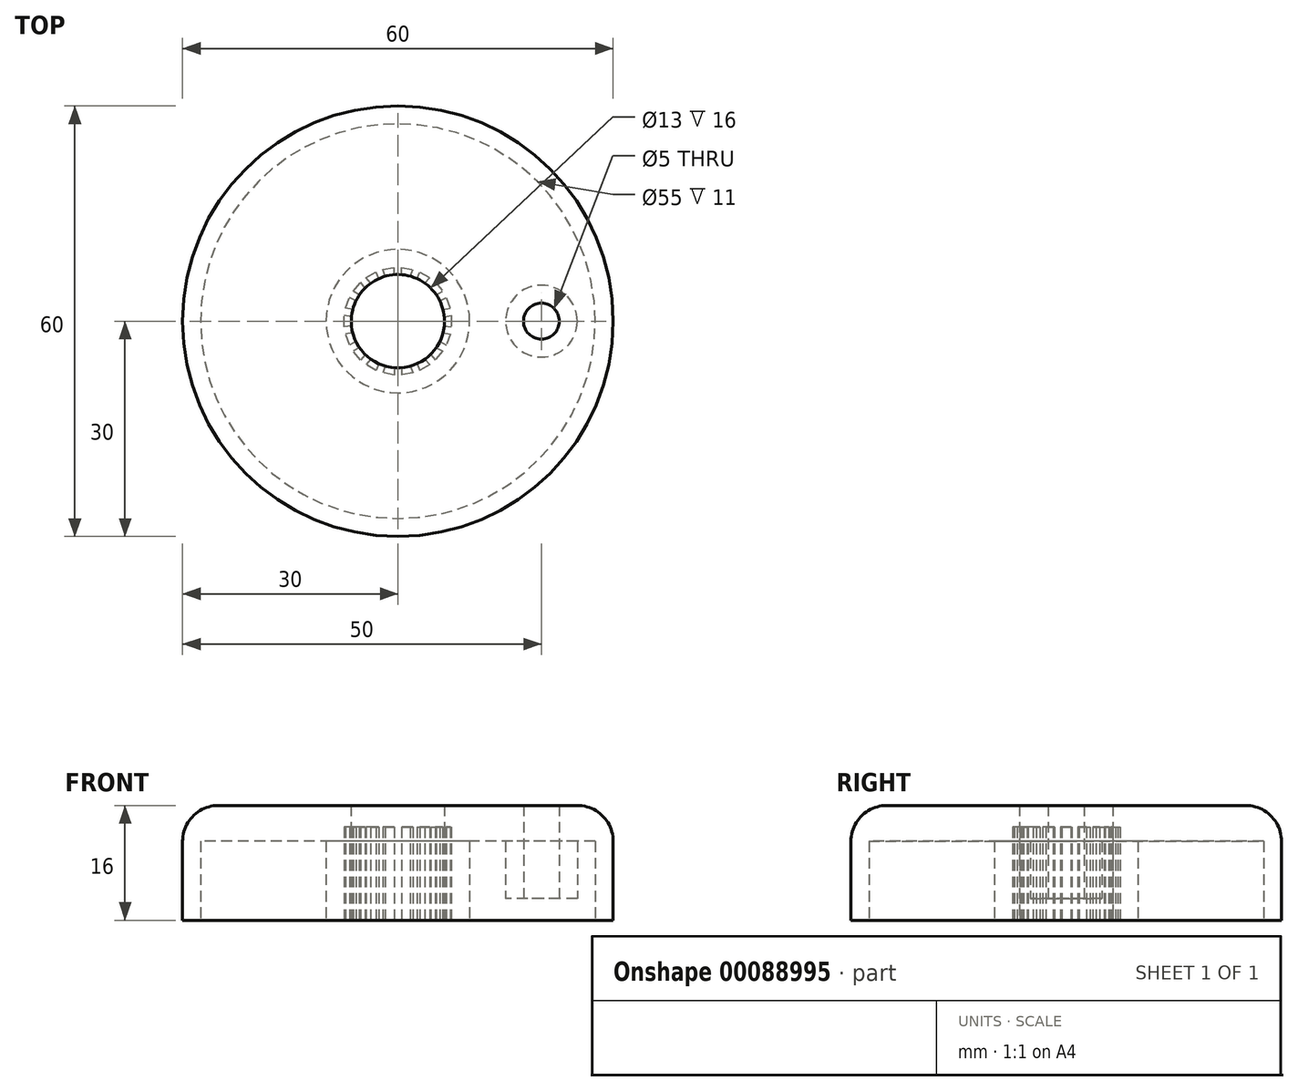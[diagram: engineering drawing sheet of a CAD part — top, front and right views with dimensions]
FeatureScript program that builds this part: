
annotation { "Feature Type Name" : "Feature", "Feature Type Description" : "" }
export const myFeature = defineFeature(function(context is Context, id is Id, definition is map)
    precondition{}
    {
        {
            var Q0;
            Q0=qCreatedBy(makeId("Top.planeOp"),FACE);
            var sketch = newSketch(context, id + "F0", { "sketchPlane" : qUnion([Q0])});
            skCircle(sketch, "E0", {"center": v(0, 0) * mm, "radius": 7.5 * mm, "construction": true});
            skLineSegment(sketch, "E1", {"start": v(0, 0) * mm, "end": v(0, 7.5) * mm, "construction": true});
            skLineSegment(sketch, "E2", {"start": v(0.5, 6.48) * mm, "end": v(0.5, 7.48) * mm});
            skLineSegment(sketch, "E3.MirrorCS", {"start": v(-0.5, 6.48) * mm, "end": v(-0.5, 7.48) * mm});
            skCircle(sketch, "E4.0", {"center": v(0, 0) * mm, "radius": 6.5 * mm, "construction": true});
            skLineSegment(sketch, "E5", {"start": v(-0.5, 6.48) * mm, "end": v(0.5, 6.48) * mm});
            skPoint(sketch, "E6.orphan", {"position": v(-0.5, 5.89) * mm});
            skPoint(sketch, "E7.orphan", {"position": v(0.5, 5.89) * mm});
            skPoint(sketch, "E8.orphan", {"position": v(0.5, 8.94) * mm});
            skPoint(sketch, "E9.orphan", {"position": v(-0.5, 8.94) * mm});
            skLineSegment(sketch, "E10.1.0", {"start": v(1.75, 6.26) * mm, "end": v(2.09, 7.2) * mm});
            skLineSegment(sketch, "E10.1.1", {"start": v(1.75, 6.26) * mm, "end": v(2.69, 5.92) * mm});
            skLineSegment(sketch, "E10.1.2", {"start": v(2.69, 5.92) * mm, "end": v(3.03, 6.86) * mm});
            skLineSegment(sketch, "E10.2.0", {"start": v(3.78, 5.29) * mm, "end": v(4.43, 6.05) * mm});
            skLineSegment(sketch, "E10.2.1", {"start": v(3.78, 5.29) * mm, "end": v(4.55, 4.64) * mm});
            skLineSegment(sketch, "E10.2.2", {"start": v(4.55, 4.64) * mm, "end": v(5.2, 5.41) * mm});
            skLineSegment(sketch, "E10.3.0", {"start": v(5.36, 3.67) * mm, "end": v(6.23, 4.17) * mm});
            skLineSegment(sketch, "E10.3.1", {"start": v(5.36, 3.67) * mm, "end": v(5.86, 2.8) * mm});
            skLineSegment(sketch, "E10.3.2", {"start": v(5.86, 2.8) * mm, "end": v(6.73, 3.3) * mm});
            skLineSegment(sketch, "E10.4.0", {"start": v(6.3, 1.62) * mm, "end": v(7.28, 1.8) * mm});
            skLineSegment(sketch, "E10.4.1", {"start": v(6.3, 1.62) * mm, "end": v(6.47, 0.63) * mm});
            skLineSegment(sketch, "E10.4.2", {"start": v(6.47, 0.63) * mm, "end": v(7.46, 0.8) * mm});
            skLineSegment(sketch, "E10.5.0", {"start": v(6.47, -0.63) * mm, "end": v(7.46, -0.8) * mm});
            skLineSegment(sketch, "E10.5.1", {"start": v(6.47, -0.63) * mm, "end": v(6.3, -1.62) * mm});
            skLineSegment(sketch, "E10.5.2", {"start": v(6.3, -1.62) * mm, "end": v(7.28, -1.8) * mm});
            skLineSegment(sketch, "E10.6.0", {"start": v(5.86, -2.8) * mm, "end": v(6.73, -3.3) * mm});
            skLineSegment(sketch, "E10.6.1", {"start": v(5.86, -2.8) * mm, "end": v(5.36, -3.67) * mm});
            skLineSegment(sketch, "E10.6.2", {"start": v(5.36, -3.67) * mm, "end": v(6.23, -4.17) * mm});
            skLineSegment(sketch, "E10.7.0", {"start": v(4.55, -4.64) * mm, "end": v(5.2, -5.41) * mm});
            skLineSegment(sketch, "E10.7.1", {"start": v(4.55, -4.64) * mm, "end": v(3.78, -5.29) * mm});
            skLineSegment(sketch, "E10.7.2", {"start": v(3.78, -5.29) * mm, "end": v(4.43, -6.05) * mm});
            skLineSegment(sketch, "E10.8.0", {"start": v(2.69, -5.92) * mm, "end": v(3.03, -6.86) * mm});
            skLineSegment(sketch, "E10.8.1", {"start": v(2.69, -5.92) * mm, "end": v(1.75, -6.26) * mm});
            skLineSegment(sketch, "E10.8.2", {"start": v(1.75, -6.26) * mm, "end": v(2.09, -7.2) * mm});
            skLineSegment(sketch, "E10.9.0", {"start": v(0.5, -6.48) * mm, "end": v(0.5, -7.48) * mm});
            skLineSegment(sketch, "E10.9.1", {"start": v(0.5, -6.48) * mm, "end": v(-0.5, -6.48) * mm});
            skLineSegment(sketch, "E10.9.2", {"start": v(-0.5, -6.48) * mm, "end": v(-0.5, -7.48) * mm});
            skLineSegment(sketch, "E10.10.0", {"start": v(-1.75, -6.26) * mm, "end": v(-2.09, -7.2) * mm});
            skLineSegment(sketch, "E10.10.1", {"start": v(-1.75, -6.26) * mm, "end": v(-2.69, -5.92) * mm});
            skLineSegment(sketch, "E10.10.2", {"start": v(-2.69, -5.92) * mm, "end": v(-3.03, -6.86) * mm});
            skLineSegment(sketch, "E10.11.0", {"start": v(-3.78, -5.29) * mm, "end": v(-4.43, -6.05) * mm});
            skLineSegment(sketch, "E10.11.1", {"start": v(-3.78, -5.29) * mm, "end": v(-4.55, -4.64) * mm});
            skLineSegment(sketch, "E10.11.2", {"start": v(-4.55, -4.64) * mm, "end": v(-5.2, -5.41) * mm});
            skLineSegment(sketch, "E10.12.0", {"start": v(-5.36, -3.67) * mm, "end": v(-6.23, -4.17) * mm});
            skLineSegment(sketch, "E10.12.1", {"start": v(-5.36, -3.67) * mm, "end": v(-5.86, -2.8) * mm});
            skLineSegment(sketch, "E10.12.2", {"start": v(-5.86, -2.8) * mm, "end": v(-6.73, -3.3) * mm});
            skLineSegment(sketch, "E10.13.0", {"start": v(-6.3, -1.62) * mm, "end": v(-7.28, -1.8) * mm});
            skLineSegment(sketch, "E10.13.1", {"start": v(-6.3, -1.62) * mm, "end": v(-6.47, -0.63) * mm});
            skLineSegment(sketch, "E10.13.2", {"start": v(-6.47, -0.63) * mm, "end": v(-7.46, -0.8) * mm});
            skLineSegment(sketch, "E10.14.0", {"start": v(-6.47, 0.63) * mm, "end": v(-7.46, 0.8) * mm});
            skLineSegment(sketch, "E10.14.1", {"start": v(-6.47, 0.63) * mm, "end": v(-6.3, 1.62) * mm});
            skLineSegment(sketch, "E10.14.2", {"start": v(-6.3, 1.62) * mm, "end": v(-7.28, 1.8) * mm});
            skLineSegment(sketch, "E10.15.0", {"start": v(-5.86, 2.8) * mm, "end": v(-6.73, 3.3) * mm});
            skLineSegment(sketch, "E10.15.1", {"start": v(-5.86, 2.8) * mm, "end": v(-5.36, 3.67) * mm});
            skLineSegment(sketch, "E10.15.2", {"start": v(-5.36, 3.67) * mm, "end": v(-6.23, 4.17) * mm});
            skLineSegment(sketch, "E10.16.0", {"start": v(-4.55, 4.64) * mm, "end": v(-5.2, 5.41) * mm});
            skLineSegment(sketch, "E10.16.1", {"start": v(-4.55, 4.64) * mm, "end": v(-3.78, 5.29) * mm});
            skLineSegment(sketch, "E10.16.2", {"start": v(-3.78, 5.29) * mm, "end": v(-4.43, 6.05) * mm});
            skLineSegment(sketch, "E10.17.0", {"start": v(-2.69, 5.92) * mm, "end": v(-3.03, 6.86) * mm});
            skLineSegment(sketch, "E10.17.1", {"start": v(-2.69, 5.92) * mm, "end": v(-1.75, 6.26) * mm});
            skLineSegment(sketch, "E10.17.2", {"start": v(-1.75, 6.26) * mm, "end": v(-2.09, 7.2) * mm});
            skLineSegment(sketch, "E10.anchor1", {"start": v(0, 0) * mm, "end": v(-0.5, 6.48) * mm, "construction": true});
            skLineSegment(sketch, "E10.anchor2", {"start": v(0, 0) * mm, "end": v(-2.69, 5.92) * mm, "construction": true});
            skLineSegment(sketch, "E11", {"start": v(-4.43, 6.05) * mm, "end": v(-3.03, 6.86) * mm});
            skLineSegment(sketch, "E12", {"start": v(-2.09, 7.2) * mm, "end": v(-0.5, 7.48) * mm});
            skLineSegment(sketch, "E13", {"start": v(0.5, 7.48) * mm, "end": v(2.09, 7.2) * mm});
            skLineSegment(sketch, "E14", {"start": v(3.03, 6.86) * mm, "end": v(4.43, 6.05) * mm});
            skLineSegment(sketch, "E15", {"start": v(5.2, 5.41) * mm, "end": v(6.23, 4.17) * mm});
            skLineSegment(sketch, "E16", {"start": v(6.73, 3.3) * mm, "end": v(7.28, 1.8) * mm});
            skLineSegment(sketch, "E17", {"start": v(7.46, 0.8) * mm, "end": v(7.46, -0.8) * mm});
            skLineSegment(sketch, "E18", {"start": v(7.28, -1.8) * mm, "end": v(6.73, -3.3) * mm});
            skLineSegment(sketch, "E19", {"start": v(6.23, -4.17) * mm, "end": v(5.2, -5.41) * mm});
            skLineSegment(sketch, "E20", {"start": v(4.43, -6.05) * mm, "end": v(3.03, -6.86) * mm});
            skLineSegment(sketch, "E21", {"start": v(2.09, -7.2) * mm, "end": v(0.5, -7.48) * mm});
            skLineSegment(sketch, "E22", {"start": v(-0.5, -7.48) * mm, "end": v(-2.09, -7.2) * mm});
            skLineSegment(sketch, "E23", {"start": v(-3.03, -6.86) * mm, "end": v(-4.43, -6.05) * mm});
            skLineSegment(sketch, "E24", {"start": v(-5.2, -5.41) * mm, "end": v(-6.23, -4.17) * mm});
            skLineSegment(sketch, "E25", {"start": v(-6.73, -3.3) * mm, "end": v(-7.28, -1.8) * mm});
            skLineSegment(sketch, "E26", {"start": v(-7.46, -0.8) * mm, "end": v(-7.46, 0.8) * mm});
            skLineSegment(sketch, "E27", {"start": v(-7.28, 1.8) * mm, "end": v(-6.73, 3.3) * mm});
            skLineSegment(sketch, "E28", {"start": v(-6.23, 4.17) * mm, "end": v(-5.2, 5.41) * mm});
            skSolve(sketch);
        }
        {
            var Q0;
            Q0=qCreatedBy(makeId("Top.planeOp"),FACE);
            var sketch = newSketch(context, id + "F1", { "sketchPlane" : qUnion([Q0])});
            skCircle(sketch, "E29", {"center": v(0, 0) * mm, "radius": 30 * mm});
            skSolve(sketch);
        }
        {
            var Q0;
            Q0 = qSketchRegion(id + "F1", true);
            extrude(context, id + "F2", {"entities" : qUnion([Q0]), "depth" : 16 * mm});
        }
        {
            var Q0;
            Q0=makeQuery(id+"F0.imprint","IMPRINT",FACE,{"disambiguationData":[TD([[makeQuery(id+"F0.imprint","IMPRINT",EDGE,{"derivedFrom":sQuery(id+"F0.wireOp",EDGE,"E2")}),-1.0]])]});
            extrude(context, id + "F3", {"entities" : qUnion([Q0]), "operationType" : NewBodyOperationType.REMOVE, "depth" : 13 * mm});
        }
        {
            var Q0;
            Q0=qCreatedBy(makeId("Top.planeOp"),FACE);
            var sketch = newSketch(context, id + "F4", { "sketchPlane" : qUnion([Q0])});
            skCircle(sketch, "E30", {"center": v(0, 0) * mm, "radius": 6.5 * mm});
            skSolve(sketch);
        }
        {
            var Q0;
            Q0=makeQuery(id+"F4.imprint","IMPRINT",FACE,{"disambiguationData":[TD([[makeQuery(id+"F4.imprint","IMPRINT",EDGE,{"derivedFrom":sQuery(id+"F4.wireOp",EDGE,"E30")}),1.0]])]});
            extrude(context, id + "F5", {"entities" : qUnion([Q0]), "operationType" : NewBodyOperationType.REMOVE, "endBound" : BoundingType.THROUGH_ALL, "depth" : 25 * mm});
        }
        {
            var Q0;
            Q0=qCreatedBy(makeId("Top.planeOp"),FACE);
            var sketch = newSketch(context, id + "F6", { "sketchPlane" : qUnion([Q0])});
            skCircle(sketch, "E31", {"center": v(20, 0) * mm, "radius": 2.5 * mm});
            skSolve(sketch);
        }
        {
            var Q0;
            Q0=makeQuery(id+"F6.imprint","IMPRINT",FACE,{"disambiguationData":[TD([[makeQuery(id+"F6.imprint","IMPRINT",EDGE,{"derivedFrom":sQuery(id+"F6.wireOp",EDGE,"E31")}),1.0]])]});
            extrude(context, id + "F7", {"entities" : qUnion([Q0]), "operationType" : NewBodyOperationType.REMOVE, "endBound" : BoundingType.THROUGH_ALL, "depth" : 25 * mm});
        }
        {
            var Q0;
            Q0=makeQuery(id+"F2.opExtrude","CAP_EDGE",EDGE,{"disambiguationData":[OSD([sQuery(id+"F1.wireOp",EDGE,"E29")])],"isStart":false});
            fillet(context, id + "F8", {"entities" : qUnion([Q0]), "radius" : 5 * mm, "tangentPropagation" : true, "allowEdgeOverflow" : false});
        }
        {
            var Q0;
            Q0=qCreatedBy(makeId("Top.planeOp"),FACE);
            var sketch = newSketch(context, id + "F9", { "sketchPlane" : qUnion([Q0])});
            skCircle(sketch, "E32.0", {"center": v(0, 0) * mm, "radius": 27.5 * mm});
            skCircle(sketch, "E33.0", {"center": v(20, 0) * mm, "radius": 5 * mm});
            skCircle(sketch, "E34", {"center": v(0, 0) * mm, "radius": 10 * mm});
            skSolve(sketch);
        }
        {
            var Q0;
            Q0=makeQuery(id+"F9.imprint","IMPRINT",FACE,{"disambiguationData":[TD([[makeQuery(id+"F9.imprint","IMPRINT",EDGE,{"derivedFrom":sQuery(id+"F9.wireOp",EDGE,"E32.0")}),1.0]])]});
            extrude(context, id + "F10", {"entities" : qUnion([Q0]), "operationType" : NewBodyOperationType.REMOVE, "depth" : 11 * mm});
        }
        {
            var Q0;
            Q0=makeQuery(id+"F10.boolean.opBoolean","SPLIT",FACE,{"disambiguationData":[TD([makeQuery(id+"F7.boolean.opBoolean","COPY",FACE,{"derivedFrom":makeQuery(id+"F7.opExtrude","SWEPT_FACE",FACE,{"disambiguationData":[OSD([sQuery(id+"F6.wireOp",EDGE,"E31")])]})})])],"derivedFrom":makeQuery(id+"F2.opExtrude","CAP_FACE",FACE,{"disambiguationData":[OSD([sQuery(id+"F1.wireOp",EDGE,"E29")])],"isStart":true})});
            extrude(context, id + "F11", {"entities" : qUnion([Q0]), "operationType" : NewBodyOperationType.REMOVE, "oppositeDirection" : true, "depth" : 3 * mm});
        }
    });
